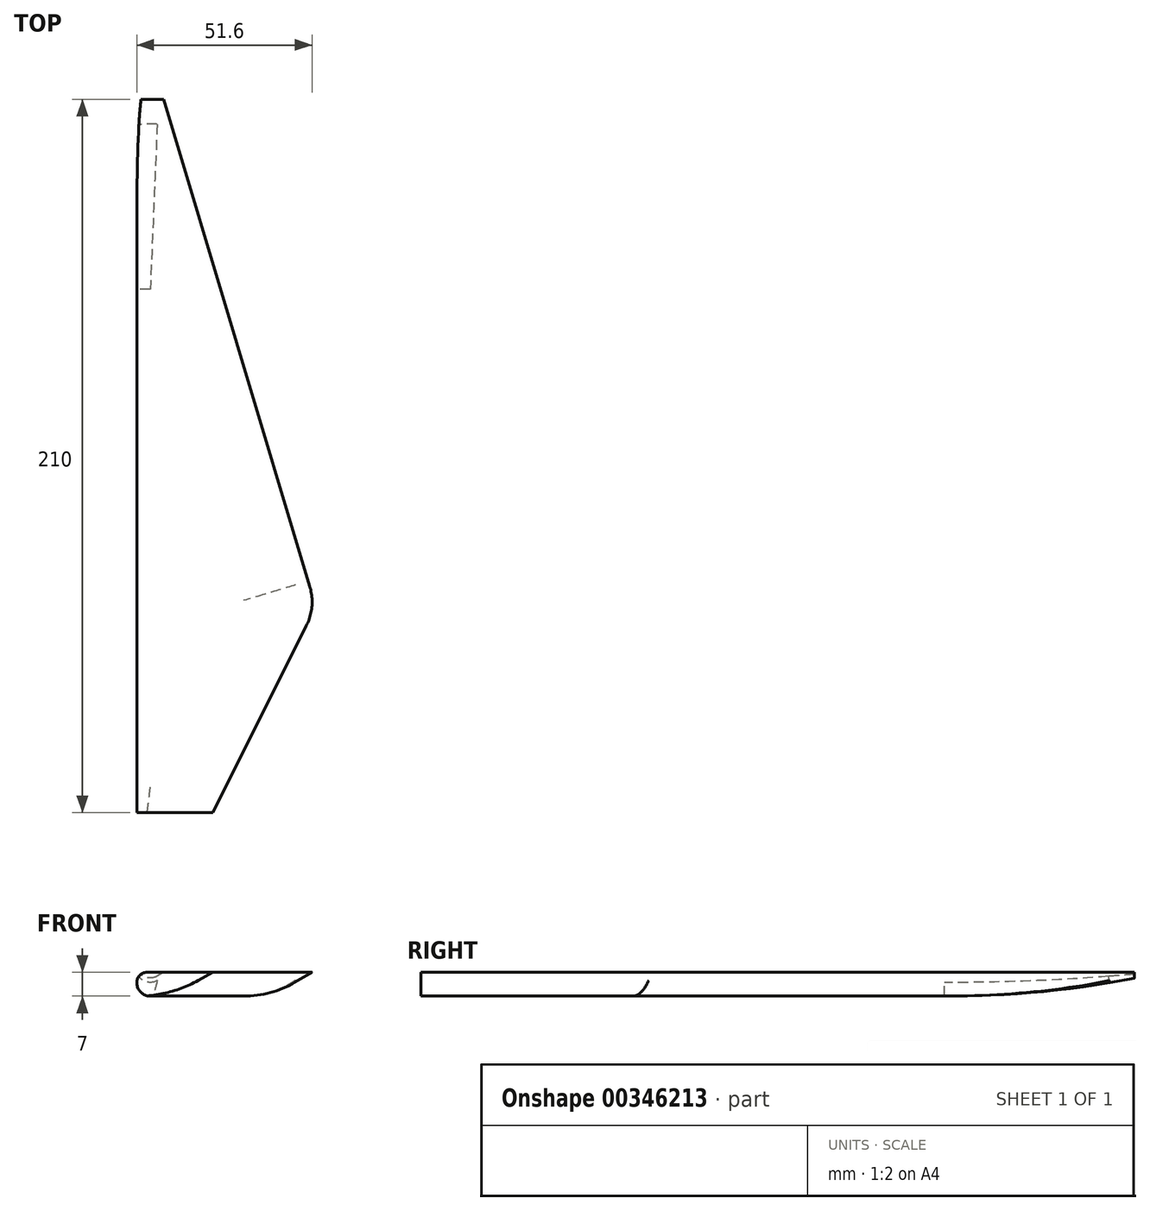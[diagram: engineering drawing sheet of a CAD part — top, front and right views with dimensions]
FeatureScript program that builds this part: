
annotation { "Feature Type Name" : "Feature", "Feature Type Description" : "" }
export const myFeature = defineFeature(function(context is Context, id is Id, definition is map)
    precondition{}
    {
        {
            var Q0;
            Q0=qCreatedBy(makeId("Top.planeOp"),FACE);
            var sketch = newSketch(context, id + "F0", { "sketchPlane" : qUnion([Q0])});
            skLineSegment(sketch, "E0.bottom", {"start": v(-35.59, 101.3) * mm, "end": v(24.41, 101.3) * mm});
            skLineSegment(sketch, "E0.top", {"start": v(-35.59, -108.7) * mm, "end": v(24.41, -108.7) * mm});
            skLineSegment(sketch, "E0.left", {"start": v(-35.59, 101.3) * mm, "end": v(-35.59, -108.7) * mm});
            skLineSegment(sketch, "E0.right", {"start": v(24.41, 101.3) * mm, "end": v(24.41, -108.7) * mm});
            skLineSegment(sketch, "E1", {"start": v(-20.59, 101.3) * mm, "end": v(24.41, -48.7) * mm});
            skLineSegment(sketch, "E2", {"start": v(24.41, -48.7) * mm, "end": v(-5.59, -108.7) * mm});
            skSolve(sketch);
        }
        {
            var Q0;
            {var subQ0=sQuery(id+"F0.wireOp",EDGE,"E0.left");Q0=makeQuery(id+"F0.imprint","IMPRINT",FACE,{"disambiguationData":[TD([[makeQuery(id+"F0.imprint","IMPRINT",EDGE,{"derivedFrom":subQ0}),1.0]])]});}
            extrude(context, id + "F1", {"entities" : qUnion([Q0]), "depth" : 7 * mm});
        }
        {
            var Q0;
            Q0=makeQuery(id+"F1.opExtrude","CAP_EDGE",EDGE,{"disambiguationData":[OSD([sQuery(id+"F0.wireOp",EDGE,"E1")])],"isStart":true});
            chamfer(context, id + "F2", {"entities" : qUnion([Q0]), "chamferType" : ChamferType.OFFSET_ANGLE, "width" : 18 * mm, "oppositeDirection" : false, "angle" : 32 * degree, "tangentPropagation" : true});
        }
        {
            var Q0;
            Q0=makeQuery(id+"F1.opExtrude","CAP_EDGE",EDGE,{"disambiguationData":[OSD([sQuery(id+"F0.wireOp",EDGE,"E2")])],"isStart":true});
            chamfer(context, id + "F3", {"entities" : qUnion([Q0]), "chamferType" : ChamferType.OFFSET_ANGLE, "width" : 18 * mm, "oppositeDirection" : false, "angle" : 32 * degree, "tangentPropagation" : true});
        }
        {
            var Q0;
            {var subQ0=sQuery(id+"F0.wireOp",EDGE,"E1");Q0=makeQuery(id+"F2.opChamfer","BLEND_EDGE",EDGE,{"blendedFrom":[makeQuery(id+"F1.opExtrude","CAP_EDGE",EDGE,{"disambiguationData":[OSD([subQ0])],"isStart":true}),makeQuery(id+"F1.opExtrude","CAP_FACE",FACE,{"disambiguationData":[OSD([sQuery(id+"F0.wireOp",EDGE,"E0.bottom"),sQuery(id+"F0.wireOp",EDGE,"E0.top"),sQuery(id+"F0.wireOp",EDGE,"E0.left"),subQ0,sQuery(id+"F0.wireOp",EDGE,"E2")])],"isStart":true})],"blendedInto":[makeQuery(id+"F1.opExtrude","CAP_FACE",FACE,{"disambiguationData":[OSD([sQuery(id+"F0.wireOp",EDGE,"E0.bottom"),sQuery(id+"F0.wireOp",EDGE,"E0.top"),sQuery(id+"F0.wireOp",EDGE,"E0.left"),subQ0,sQuery(id+"F0.wireOp",EDGE,"E2")])],"isStart":true})]});}
            fillet(context, id + "F4", {"entities" : qUnion([Q0]), "radius" : 30 * mm, "tangentPropagation" : true, "allowEdgeOverflow" : false});
        }
        {
            var Q0;
            {var subQ0=sQuery(id+"F0.wireOp",EDGE,"E2");Q0=makeQuery(id+"F3.opChamfer","BLEND_EDGE",EDGE,{"blendedFrom":[makeQuery(id+"F1.opExtrude","CAP_EDGE",EDGE,{"disambiguationData":[OSD([subQ0])],"isStart":true}),makeQuery(id+"F1.opExtrude","CAP_FACE",FACE,{"disambiguationData":[OSD([sQuery(id+"F0.wireOp",EDGE,"E0.bottom"),sQuery(id+"F0.wireOp",EDGE,"E0.top"),sQuery(id+"F0.wireOp",EDGE,"E0.left"),sQuery(id+"F0.wireOp",EDGE,"E1"),subQ0])],"isStart":true})],"blendedInto":[makeQuery(id+"F1.opExtrude","CAP_FACE",FACE,{"disambiguationData":[OSD([sQuery(id+"F0.wireOp",EDGE,"E0.bottom"),sQuery(id+"F0.wireOp",EDGE,"E0.top"),sQuery(id+"F0.wireOp",EDGE,"E0.left"),sQuery(id+"F0.wireOp",EDGE,"E1"),subQ0])],"isStart":true})]});}
            fillet(context, id + "F5", {"entities" : qUnion([Q0]), "radius" : 30 * mm, "tangentPropagation" : true, "allowEdgeOverflow" : false});
        }
        {
            var Q0;
            Q0=makeQuery(id+"F1.opExtrude","CAP_EDGE",EDGE,{"disambiguationData":[OSD([sQuery(id+"F0.wireOp",EDGE,"E0.left")])],"isStart":false});
            fillet(context, id + "F6", {"entities" : qUnion([Q0]), "radius" : 3 * mm, "tangentPropagation" : true, "allowEdgeOverflow" : false});
        }
        {
            var Q0;
            Q0=makeQuery(id+"F1.opExtrude","CAP_EDGE",EDGE,{"disambiguationData":[OSD([sQuery(id+"F0.wireOp",EDGE,"E0.left")])],"isStart":true});
            fillet(context, id + "F7", {"entities" : qUnion([Q0]), "radius" : 4 * mm, "tangentPropagation" : true, "allowEdgeOverflow" : false});
        }
    });
